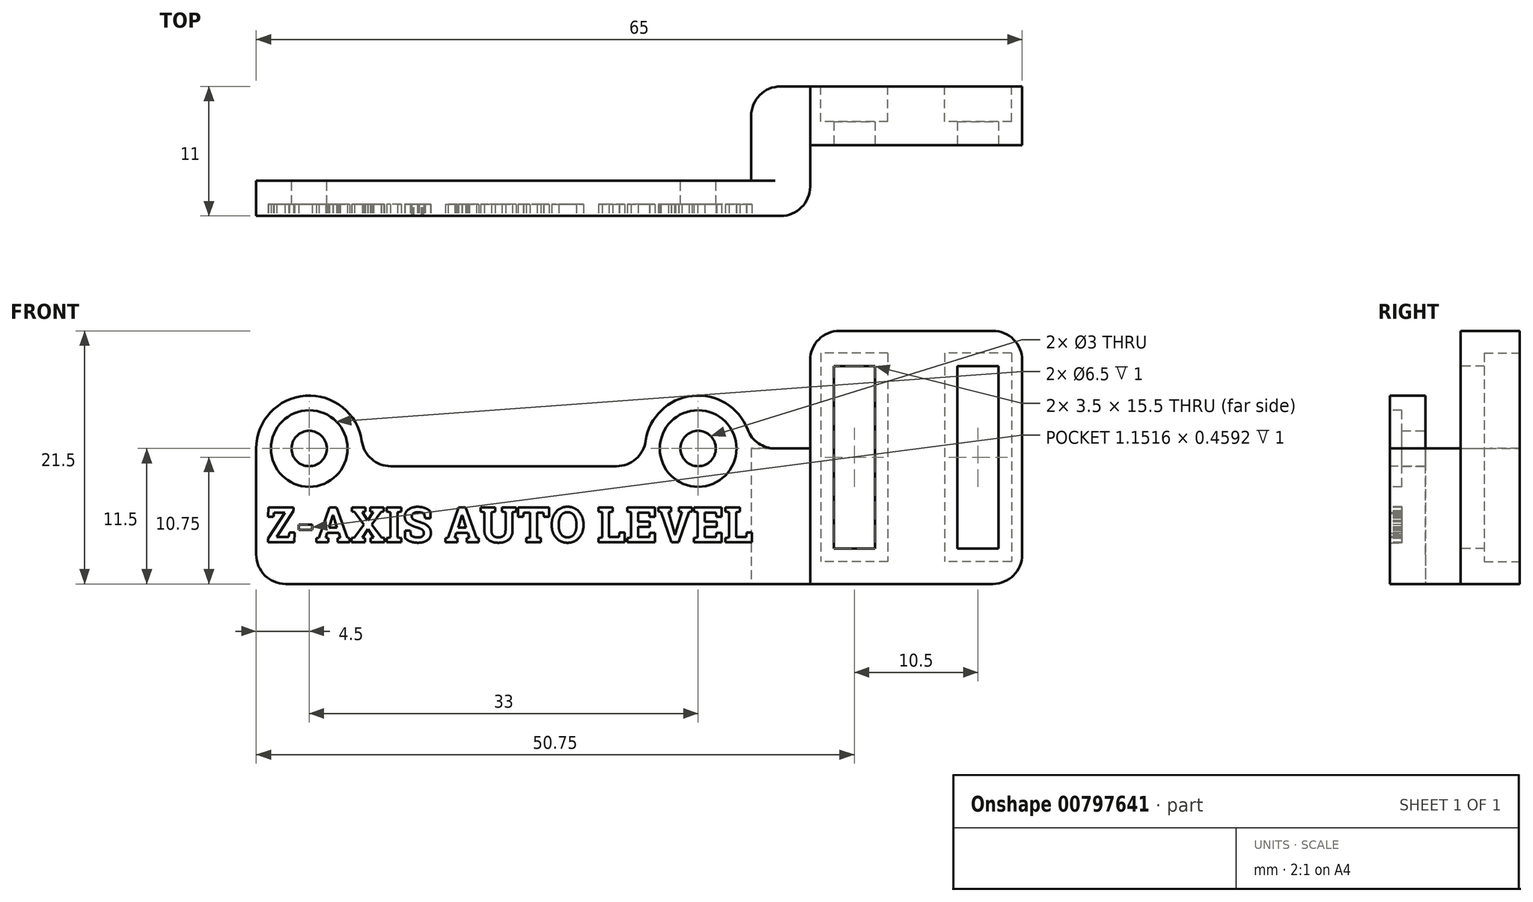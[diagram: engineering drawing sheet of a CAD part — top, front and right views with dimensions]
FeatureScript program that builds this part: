
annotation { "Feature Type Name" : "Feature", "Feature Type Description" : "" }
export const myFeature = defineFeature(function(context is Context, id is Id, definition is map)
    precondition{}
    {
        {
            var Q0;
            Q0=qCreatedBy(makeId("Front.planeOp"),FACE);
            var sketch = newSketch(context, id + "F0", { "sketchPlane" : qUnion([Q0])});
            skLineSegment(sketch, "E0.bottom", {"start": v(0, 0) * mm, "end": v(-42, 0) * mm});
            skLineSegment(sketch, "E0.top", {"start": v(-9, 10) * mm, "end": v(-33, 10) * mm});
            skLineSegment(sketch, "E0.left", {"start": v(0, 0) * mm, "end": v(0, 10) * mm});
            skLineSegment(sketch, "E0.right", {"start": v(-42, 0) * mm, "end": v(-42, 10) * mm});
            skCircle(sketch, "E1", {"center": v(-37.5, 11.5) * mm, "radius": 1.5 * mm});
            skCircle(sketch, "E2", {"center": v(-4.5, 11.5) * mm, "radius": 1.5 * mm});
            skLineSegment(sketch, "E3", {"start": v(-42, 10) * mm, "end": v(-42, 11.5) * mm});
            skLineSegment(sketch, "E4", {"start": v(-33, 10) * mm, "end": v(-33, 11.5) * mm});
            skLineSegment(sketch, "E5", {"start": v(-9, 10) * mm, "end": v(-9, 11.5) * mm});
            skLineSegment(sketch, "E6", {"start": v(0, 10) * mm, "end": v(0, 11.5) * mm});
            skArc(sketch, "E7", {"start": v(-33, 11.5) * mm, "mid": v(-37.5, 16) * mm, "end": v(-42, 11.5) * mm});
            skArc(sketch, "E8", {"start": v(0, 11.5) * mm, "mid": v(-4.5, 16) * mm, "end": v(-9, 11.5) * mm});
            skLineSegment(sketch, "E9.bottom", {"start": v(0, 0) * mm, "end": v(5, 0) * mm});
            skLineSegment(sketch, "E9.top", {"start": v(0, 11.5) * mm, "end": v(5, 11.5) * mm});
            skLineSegment(sketch, "E9.right", {"start": v(5, 0) * mm, "end": v(5, 11.5) * mm});
            skSolve(sketch);
        }
        {
            var Q0;
            Q0=makeQuery(id+"F0.imprint","IMPRINT",FACE,{"disambiguationData":[TD([[makeQuery(id+"F0.imprint","IMPRINT",EDGE,{"derivedFrom":sQuery(id+"F0.wireOp",EDGE,"E0.bottom")}),-1.0]])]});
            var Q1;
            Q1=makeQuery(id+"F0.imprint","IMPRINT",FACE,{"disambiguationData":[TD([[makeQuery(id+"F0.imprint","IMPRINT",EDGE,{"derivedFrom":sQuery(id+"F0.wireOp",EDGE,"E0.left")}),-1.0]])]});
            extrude(context, id + "F1", {"entities" : qUnion([Q0, Q1]), "depth" : 3 * mm, "offsetDistance" : 25 * mm});
        }
        {
            var Q0;
            Q0=qCreatedBy(makeId("Top.planeOp"),FACE);
            var sketch = newSketch(context, id + "F2", { "sketchPlane" : qUnion([Q0])});
            skLineSegment(sketch, "E10.bottom", {"start": v(0, 0) * mm, "end": v(5, 0) * mm});
            skLineSegment(sketch, "E10.top", {"start": v(0, 8) * mm, "end": v(5, 8) * mm});
            skLineSegment(sketch, "E10.left", {"start": v(0, 0) * mm, "end": v(0, 8) * mm});
            skLineSegment(sketch, "E10.right", {"start": v(5, 0) * mm, "end": v(5, 8) * mm});
            skLineSegment(sketch, "E11.bottom", {"start": v(5, 8) * mm, "end": v(23, 8) * mm});
            skLineSegment(sketch, "E11.top", {"start": v(5, 3) * mm, "end": v(23, 3) * mm});
            skLineSegment(sketch, "E11.left", {"start": v(5, 8) * mm, "end": v(5, 3) * mm});
            skLineSegment(sketch, "E11.right", {"start": v(23, 8) * mm, "end": v(23, 3) * mm});
            skSolve(sketch);
        }
        {
            var Q0;
            {var subQ3=sQuery(id+"F2.wireOp",EDGE,"E10.bottom");Q0=makeQuery(id+"F2.imprint","IMPRINT",FACE,{"disambiguationData":[TD([[makeQuery(id+"F2.imprint","IMPRINT",EDGE,{"derivedFrom":subQ3}),1.0]])]});}
            var Q1;
            {var subQ0=sQuery(id+"F2.wireOp",EDGE,"E11.bottom");Q1=makeQuery(id+"F2.imprint","IMPRINT",FACE,{"disambiguationData":[TD([[makeQuery(id+"F2.imprint","IMPRINT",EDGE,{"derivedFrom":subQ0}),-1.0]])]});}
            var Q2;
            Q2=makeQuery(id+"F1.opExtrude","SWEPT_FACE",FACE,{"disambiguationData":[OSD([sQuery(id+"F0.wireOp",EDGE,"E9.top")])]});
            extrude(context, id + "F3", {"entities" : qUnion([Q0, Q1]), "operationType" : NewBodyOperationType.ADD, "endBound" : BoundingType.UP_TO_SURFACE, "depth" : 10 * mm, "endBoundEntityFace" : qUnion([Q2]), "offsetDistance" : 25 * mm});
        }
        {
            var Q0;
            {var subQ0=sQuery(id+"F0.wireOp",EDGE,"E9.top");Q0=makeQuery(id+"F3.boolean.opBoolean","MERGE",FACE,{"derivedFrom":[makeQuery(id+"F1.opExtrude","SWEPT_FACE",FACE,{"disambiguationData":[OSD([subQ0])]}),makeQuery(id+"F3.opExtrude","CAP_FACE",FACE,{"disambiguationData":[OSD([subQ0])],"isStart":false})]});}
            var sketch = newSketch(context, id + "F4", { "sketchPlane" : qUnion([Q0])});
            skLineSegment(sketch, "E12.bottom", {"start": v(23, 3) * mm, "end": v(5, 3) * mm});
            skLineSegment(sketch, "E12.top", {"start": v(23, 8) * mm, "end": v(5, 8) * mm});
            skLineSegment(sketch, "E12.left", {"start": v(23, 3) * mm, "end": v(23, 8) * mm});
            skLineSegment(sketch, "E12.right", {"start": v(5, 3) * mm, "end": v(5, 8) * mm});
            skSolve(sketch);
        }
        {
            var Q0;
            Q0 = qSketchRegion(id + "F4", true);
            extrude(context, id + "F5", {"entities" : qUnion([Q0]), "operationType" : NewBodyOperationType.ADD, "depth" : 10 * mm, "offsetDistance" : 25 * mm});
        }
        {
            var Q0;
            Q0=makeQuery(id+"F5.opExtrude","CAP_EDGE",EDGE,{"disambiguationData":[OSD([sQuery(id+"F4.wireOp",EDGE,"E12.right")])],"isStart":true});
            var Q1;
            Q1=makeQuery(id+"F1.opExtrude","SWEPT_EDGE",EDGE,{"disambiguationData":[OSD([sQuery(id+"F0.wireOp",EDGE,"E0.top"),sQuery(id+"F0.wireOp",EDGE,"E5")])]});
            var Q2;
            Q2=makeQuery(id+"F1.opExtrude","SWEPT_EDGE",EDGE,{"disambiguationData":[OSD([sQuery(id+"F0.wireOp",EDGE,"E0.top"),sQuery(id+"F0.wireOp",EDGE,"E4")])]});
            var Q3;
            Q3=makeQuery(id+"F1.opExtrude","SWEPT_EDGE",EDGE,{"disambiguationData":[OSD([sQuery(id+"F0.wireOp",EDGE,"E6"),sQuery(id+"F0.wireOp",EDGE,"E8"),sQuery(id+"F0.wireOp",EDGE,"E9.top")])]});
            fillet(context, id + "F6", {"entities" : qUnion([Q0, Q1, Q2, Q3]), "radius" : 2.5 * mm, "tangentPropagation" : true, "allowEdgeOverflow" : false});
        }
        {
            var Q0;
            Q0=makeQuery(id+"F5.boolean.opBoolean","MERGE",FACE,{"derivedFrom":[makeQuery(id+"F3.opExtrude","SWEPT_FACE",FACE,{"disambiguationData":[OSD([sQuery(id+"F2.wireOp",EDGE,"E11.top")])]}),makeQuery(id+"F5.opExtrude","SWEPT_FACE",FACE,{"disambiguationData":[OSD([sQuery(id+"F4.wireOp",EDGE,"E12.bottom")])]})]});
            var sketch = newSketch(context, id + "F7", { "sketchPlane" : qUnion([Q0])});
            skLineSegment(sketch, "E13.bottom", {"start": v(7, 18.5) * mm, "end": v(10.5, 18.5) * mm});
            skLineSegment(sketch, "E13.top", {"start": v(7, 3) * mm, "end": v(10.5, 3) * mm});
            skLineSegment(sketch, "E13.left", {"start": v(7, 18.5) * mm, "end": v(7, 3) * mm});
            skLineSegment(sketch, "E13.right", {"start": v(10.5, 18.5) * mm, "end": v(10.5, 3) * mm});
            skLineSegment(sketch, "E14.bottom", {"start": v(17.5, 18.5) * mm, "end": v(21, 18.5) * mm});
            skLineSegment(sketch, "E14.top", {"start": v(17.5, 3) * mm, "end": v(21, 3) * mm});
            skLineSegment(sketch, "E14.left", {"start": v(17.5, 18.5) * mm, "end": v(17.5, 3) * mm});
            skLineSegment(sketch, "E14.right", {"start": v(21, 18.5) * mm, "end": v(21, 3) * mm});
            skPoint(sketch, "E15", {"position": v(8.75, 18.5) * mm});
            skPoint(sketch, "E16", {"position": v(19.25, 18.5) * mm});
            skLineSegment(sketch, "E17", {"start": v(8.75, 18.5) * mm, "end": v(19.25, 18.5) * mm, "construction": true});
            skLineSegment(sketch, "E18", {"start": v(14, 21.5) * mm, "end": v(14, 0) * mm, "construction": true});
            skPoint(sketch, "E19", {"position": v(14, 18.5) * mm});
            skLineSegment(sketch, "E20", {"start": v(8.75, 18.5) * mm, "end": v(8.75, 21.5) * mm, "construction": true});
            skLineSegment(sketch, "E21", {"start": v(8.75, 3) * mm, "end": v(8.75, 0) * mm, "construction": true});
            skSolve(sketch);
        }
        {
            var Q0;
            Q0 = qSketchRegion(id + "F7", true);
            extrude(context, id + "F8", {"entities" : qUnion([Q0]), "operationType" : NewBodyOperationType.REMOVE, "endBound" : BoundingType.THROUGH_ALL, "oppositeDirection" : true, "depth" : 25 * mm, "offsetDistance" : 25 * mm});
        }
        {
            var Q0;
            Q0=makeQuery(id+"F5.boolean.opBoolean","MERGE",FACE,{"derivedFrom":[makeQuery(id+"F3.opExtrude","SWEPT_FACE",FACE,{"disambiguationData":[OSD([sQuery(id+"F2.wireOp",EDGE,"E10.top"),sQuery(id+"F2.wireOp",EDGE,"E11.bottom")])]}),makeQuery(id+"F5.opExtrude","SWEPT_FACE",FACE,{"disambiguationData":[OSD([sQuery(id+"F4.wireOp",EDGE,"E12.top")])]})]});
            var sketch = newSketch(context, id + "F9", { "sketchPlane" : qUnion([Q0])});
            skLineSegment(sketch, "E22.bottom", {"start": v(-22.1, 19.6) * mm, "end": v(-16.4, 19.6) * mm});
            skLineSegment(sketch, "E22.top", {"start": v(-22.1, 1.9) * mm, "end": v(-16.4, 1.9) * mm});
            skLineSegment(sketch, "E22.left", {"start": v(-22.1, 19.6) * mm, "end": v(-22.1, 1.9) * mm});
            skLineSegment(sketch, "E22.right", {"start": v(-16.4, 19.6) * mm, "end": v(-16.4, 1.9) * mm});
            skLineSegment(sketch, "E23.bottom", {"start": v(-11.6, 19.6) * mm, "end": v(-5.9, 19.6) * mm});
            skLineSegment(sketch, "E23.top", {"start": v(-11.6, 1.9) * mm, "end": v(-5.9, 1.9) * mm});
            skLineSegment(sketch, "E23.left", {"start": v(-11.6, 19.6) * mm, "end": v(-11.6, 1.9) * mm});
            skLineSegment(sketch, "E23.right", {"start": v(-5.9, 19.6) * mm, "end": v(-5.9, 1.9) * mm});
            skLineSegment(sketch, "E24", {"start": v(-19.25, 18.5) * mm, "end": v(-19.25, 3) * mm, "construction": true});
            skLineSegment(sketch, "E25", {"start": v(-8.75, 3) * mm, "end": v(-8.75, 18.5) * mm, "construction": true});
            skPoint(sketch, "E26", {"position": v(-19.25, 10.75) * mm});
            skPoint(sketch, "E27", {"position": v(-8.75, 10.75) * mm});
            skLineSegment(sketch, "E28", {"start": v(-22.1, 10.75) * mm, "end": v(-16.4, 10.75) * mm, "construction": true});
            skLineSegment(sketch, "E29", {"start": v(-16.4, 10.75) * mm, "end": v(-11.6, 10.75) * mm, "construction": true});
            skLineSegment(sketch, "E30", {"start": v(-11.6, 10.75) * mm, "end": v(-5.9, 10.75) * mm, "construction": true});
            skLineSegment(sketch, "E31", {"start": v(-21, 15.56) * mm, "end": v(-22.1, 15.56) * mm, "construction": true});
            skLineSegment(sketch, "E32", {"start": v(-19.25, 19.6) * mm, "end": v(-19.25, 18.5) * mm, "construction": true});
            skSolve(sketch);
        }
        {
            var Q0;
            Q0 = qSketchRegion(id + "F9", true);
            extrude(context, id + "F10", {"entities" : qUnion([Q0]), "operationType" : NewBodyOperationType.REMOVE, "oppositeDirection" : true, "depth" : 3 * mm, "offsetDistance" : 25 * mm});
        }
        {
            var Q0;
            {var subQ0=sQuery(id+"F2.wireOp",EDGE,"E10.right");Q0=makeQuery(id+"F6.opFillet","TWEAK_EDGE",EDGE,{"derivedFrom":[makeQuery(id+"F5.boolean.opBoolean","MERGE",VERTEX,{"derivedFrom":[makeQuery(id+"F3.opExtrude","CAP_VERTEX",VERTEX,{"disambiguationData":[OSD([subQ0,sQuery(id+"F2.wireOp",EDGE,"E11.top")])],"isStart":false}),makeQuery(id+"F5.opExtrude","CAP_VERTEX",VERTEX,{"disambiguationData":[OSD([sQuery(id+"F0.wireOp",EDGE,"E9.top"),sQuery(id+"F0.wireOp",EDGE,"E9.right"),subQ0,sQuery(id+"F4.wireOp",EDGE,"E12.bottom"),sQuery(id+"F4.wireOp",EDGE,"E12.right")])],"isStart":true})]})]});}
            var Q1;
            Q1=makeQuery(id+"F3.opExtrude","SWEPT_EDGE",EDGE,{"disambiguationData":[OSD([sQuery(id+"F2.wireOp",EDGE,"E10.top"),sQuery(id+"F2.wireOp",EDGE,"E10.left")])]});
            var Q2;
            Q2=makeQuery(id+"F1.opExtrude","CAP_EDGE",EDGE,{"disambiguationData":[OSD([sQuery(id+"F0.wireOp",EDGE,"E9.right")])],"isStart":false});
            var Q3;
            Q3=makeQuery(id+"F3.opExtrude","CAP_EDGE",EDGE,{"disambiguationData":[OSD([sQuery(id+"F2.wireOp",EDGE,"E11.right")])],"isStart":true});
            var Q4;
            Q4=makeQuery(id+"F5.opExtrude","CAP_EDGE",EDGE,{"disambiguationData":[OSD([sQuery(id+"F4.wireOp",EDGE,"E12.left")])],"isStart":false});
            var Q5;
            Q5=makeQuery(id+"F5.opExtrude","CAP_EDGE",EDGE,{"disambiguationData":[OSD([sQuery(id+"F4.wireOp",EDGE,"E12.right")])],"isStart":false});
            var Q6;
            Q6=makeQuery(id+"F1.opExtrude","SWEPT_EDGE",EDGE,{"disambiguationData":[OSD([sQuery(id+"F0.wireOp",EDGE,"E0.bottom"),sQuery(id+"F0.wireOp",EDGE,"E0.right")])]});
            fillet(context, id + "F11", {"entities" : qUnion([Q0, Q1, Q2, Q3, Q4, Q5, Q6]), "radius" : 2.5 * mm, "tangentPropagation" : true, "allowEdgeOverflow" : false});
        }
        {
            var Q0;
            Q0=makeQuery(id+"F1.opExtrude","CAP_FACE",FACE,{"disambiguationData":[OSD([sQuery(id+"F0.wireOp",EDGE,"E0.bottom"),sQuery(id+"F0.wireOp",EDGE,"E0.top"),sQuery(id+"F0.wireOp",EDGE,"E0.right"),sQuery(id+"F0.wireOp",EDGE,"E1"),sQuery(id+"F0.wireOp",EDGE,"E2"),sQuery(id+"F0.wireOp",EDGE,"E3"),sQuery(id+"F0.wireOp",EDGE,"E4"),sQuery(id+"F0.wireOp",EDGE,"E5"),sQuery(id+"F0.wireOp",EDGE,"E7"),sQuery(id+"F0.wireOp",EDGE,"E8"),sQuery(id+"F0.wireOp",EDGE,"E9.bottom"),sQuery(id+"F0.wireOp",EDGE,"E9.top"),sQuery(id+"F0.wireOp",EDGE,"E9.right")])],"isStart":false});
            var sketch = newSketch(context, id + "F12", { "sketchPlane" : qUnion([Q0])});
            skLineSegment(sketch, "E33", {"start": v(-21, 10) * mm, "end": v(-21, 0) * mm, "construction": true});
            skText(sketch, "E34", { "text": "Z-AXIS AUTO LEVEL", "fontName": "RobotoSlab-Bold.ttf"});
            skPoint(sketch, "E35", {"position": v(-20.4, 6.55) * mm});
            const initialGuessF12  = {"E34": [-0.04115, 0.00354, 1, 0, 0.00301]};
            skSetInitialGuess(sketch, initialGuessF12);
            skSolve(sketch);
        }
        {
            var Q0;
            Q0 = qSketchRegion(id + "F12", true);
            extrude(context, id + "F13", {"entities" : qUnion([Q0]), "operationType" : NewBodyOperationType.REMOVE, "oppositeDirection" : true, "depth" : 1 * mm, "offsetDistance" : 25 * mm});
        }
        {
            var Q0;
            {var subQ0=sQuery(id+"F0.wireOp",EDGE,"E9.top");var subQ1=sQuery(id+"F0.wireOp",EDGE,"E5");var subQ2=sQuery(id+"F0.wireOp",EDGE,"E0.top");var subQ3=sQuery(id+"F0.wireOp",EDGE,"E3");var subQ4=sQuery(id+"F0.wireOp",EDGE,"E0.right");var subQ5=sQuery(id+"F0.wireOp",EDGE,"E2");var subQ6=sQuery(id+"F0.wireOp",EDGE,"E8");var subQ7=sQuery(id+"F0.wireOp",EDGE,"E9.bottom");var subQ8=sQuery(id+"F0.wireOp",EDGE,"E0.bottom");var subQ9=sQuery(id+"F0.wireOp",EDGE,"E9.right");var subQ10=sQuery(id+"F0.wireOp",EDGE,"E1");var subQ11=sQuery(id+"F0.wireOp",EDGE,"E4");var subQ12=sQuery(id+"F0.wireOp",EDGE,"E7");Q0=makeQuery(id+"F13.boolean.opBoolean","SPLIT",FACE,{"disambiguationData":[TD([makeQuery(id+"F1.opExtrude","SWEPT_FACE",FACE,{"disambiguationData":[OSD([subQ2])]})])],"derivedFrom":makeQuery(id+"F1.opExtrude","CAP_FACE",FACE,{"disambiguationData":[OSD([subQ8,subQ2,subQ4,subQ10,subQ5,subQ3,subQ11,subQ1,subQ12,subQ6,subQ7,subQ0,subQ9])],"isStart":false})});}
            var sketch = newSketch(context, id + "F14", { "sketchPlane" : qUnion([Q0])});
            skCircle(sketch, "E36", {"center": v(-37.5, 11.5) * mm, "radius": 3.25 * mm});
            skCircle(sketch, "E37", {"center": v(-4.5, 11.5) * mm, "radius": 3.25 * mm});
            skSolve(sketch);
        }
        {
            var Q0;
            Q0 = qSketchRegion(id + "F14", true);
            extrude(context, id + "F15", {"entities" : qUnion([Q0]), "operationType" : NewBodyOperationType.REMOVE, "oppositeDirection" : true, "depth" : 1 * mm, "offsetDistance" : 25 * mm});
        }
    });
